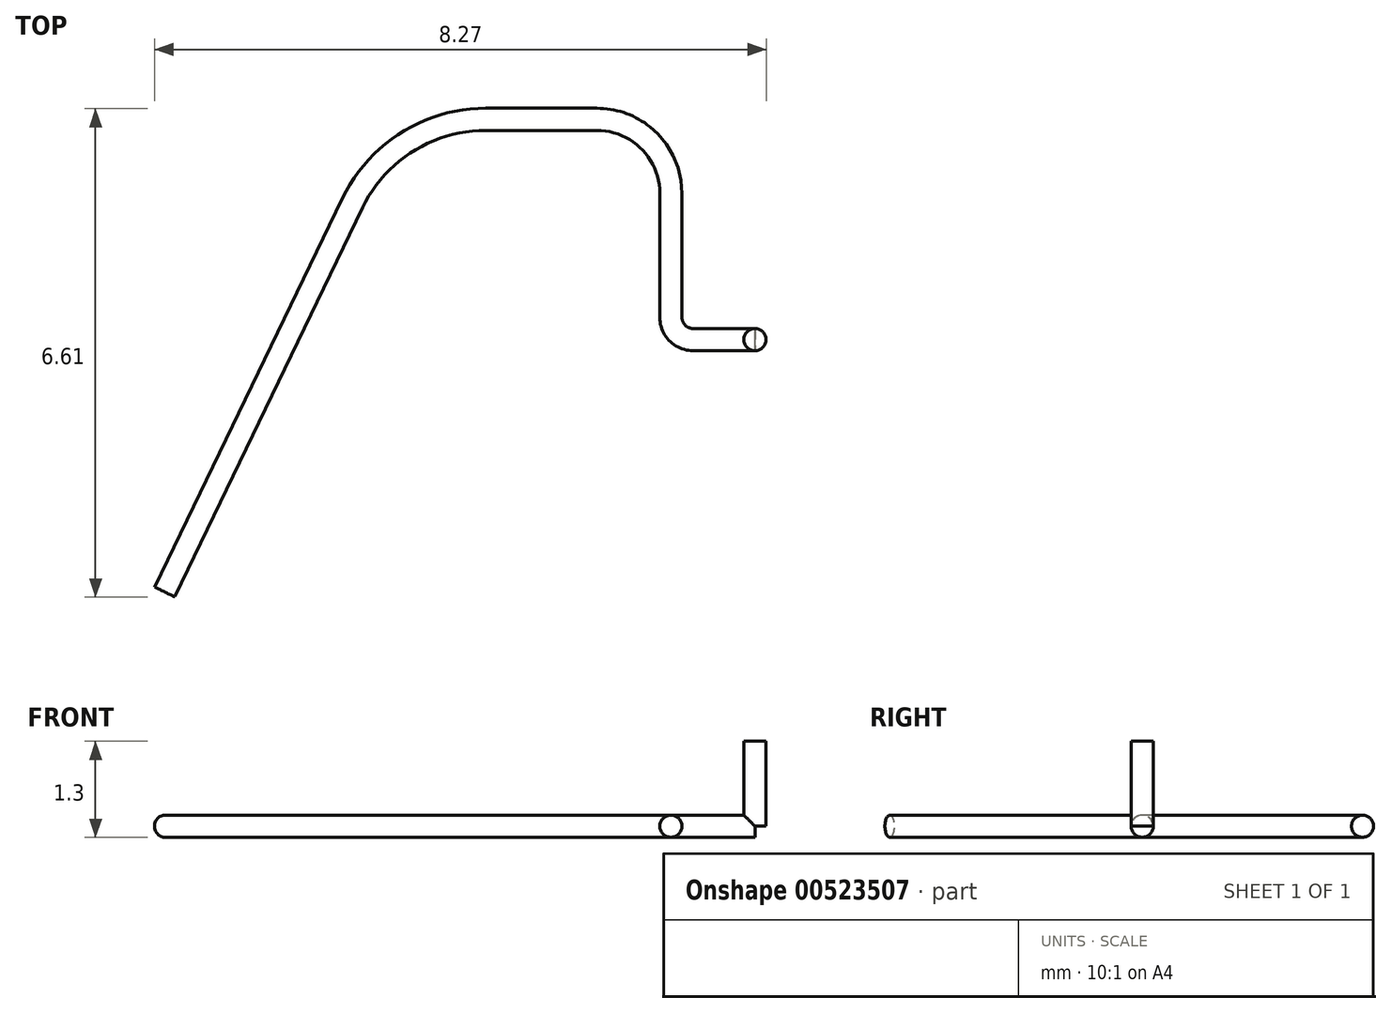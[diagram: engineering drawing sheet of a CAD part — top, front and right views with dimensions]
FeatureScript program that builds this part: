
annotation { "Feature Type Name" : "Feature", "Feature Type Description" : "" }
export const myFeature = defineFeature(function(context is Context, id is Id, definition is map)
    precondition{}
    {
        {
            var Q0;
            Q0=qCreatedBy(makeId("Front.planeOp"),FACE);
            var sketch = newSketch(context, id + "F0", { "sketchPlane" : qUnion([Q0])});
            skCircle(sketch, "E0", {"center": v(0, 0) * mm, "radius": 0.15 * mm});
            skSolve(sketch);
        }
        {
            var Q0;
            Q0=qCreatedBy(makeId("Top.planeOp"),FACE);
            var sketch = newSketch(context, id + "F1", { "sketchPlane" : qUnion([Q0])});
            skLineSegment(sketch, "E1", {"start": v(0, 0) * mm, "end": v(0, 1.08) * mm});
            skLineSegment(sketch, "E2", {"start": v(-1, 2.08) * mm, "end": v(-2.5, 2.08) * mm});
            skPoint(sketch, "E3.visualSharp", {"position": v(0, 2.08) * mm});
            skArc(sketch, "E3.filletArc", {"start": v(0, 1.08) * mm, "mid": v(-0.3, 1.8) * mm, "end": v(-1, 2.08) * mm});
            skLineSegment(sketch, "E4", {"start": v(-4.3, 0.95) * mm, "end": v(-6.85, -4.31) * mm});
            skPoint(sketch, "E5.visualSharp", {"position": v(-3.76, 2.08) * mm});
            skArc(sketch, "E5.filletArc", {"start": v(-2.5, 2.08) * mm, "mid": v(-3.57, 1.78) * mm, "end": v(-4.3, 0.95) * mm});
            skSolve(sketch);
        }
        {
            var Q0;
            Q0 = qSketchRegion(id + "F0", true);
            var Q1;
            Q1 = qConstructionFilter(qBodyType(qCreatedBy(id + "F1" ,EDGE), BodyType.WIRE), ConstructionObject.NO);
            sweep(context, id + "F2", {"profiles" : qUnion([Q0]), "path" : qUnion([Q1])});
        }
        {
            var Q0;
            Q0=qCreatedBy(makeId("Top.planeOp"),FACE);
            var sketch = newSketch(context, id + "F3", { "sketchPlane" : qUnion([Q0])});
            skLineSegment(sketch, "E6", {"start": v(0, 0) * mm, "end": v(0, -0.6) * mm});
            skLineSegment(sketch, "E7", {"start": v(0.3, -0.9) * mm, "end": v(1.14, -0.9) * mm});
            skPoint(sketch, "E8.visualSharp", {"position": v(0, -0.9) * mm});
            skArc(sketch, "E8.filletArc", {"start": v(0, -0.6) * mm, "mid": v(0.09, -0.8) * mm, "end": v(0.3, -0.9) * mm});
            skSolve(sketch);
        }
        {
            var Q0;
            Q0 = qSketchRegion(id + "F0", true);
            var Q1;
            Q1 = qConstructionFilter(qBodyType(qCreatedBy(id + "F3" ,EDGE), BodyType.WIRE), ConstructionObject.NO);
            sweep(context, id + "F4", {"operationType" : NewBodyOperationType.ADD, "profiles" : qUnion([Q0]), "path" : qUnion([Q1])});
        }
        {
            var Q0;
            Q0=makeQuery(id+"F4.opSweep","CAP_FACE",FACE,{"disambiguationData":[OSD([sQuery(id+"F0.wireOp",EDGE,"E0"),sQuery(id+"F3.wireOp",VERTEX,"E7.end")])],"isStart":false});
            var sketch = newSketch(context, id + "F5", { "sketchPlane" : qUnion([Q0])});
            skLineSegment(sketch, "E9", {"start": v(-0.9, 0) * mm, "end": v(-0.9, 1.15) * mm});
            skSolve(sketch);
        }
        {
            var Q0;
            Q0=qCreatedBy(makeId("Top.planeOp"),FACE);
            var sketch = newSketch(context, id + "F6", { "sketchPlane" : qUnion([Q0])});
            skCircle(sketch, "E10", {"center": v(1.14, -0.9) * mm, "radius": 0.15 * mm});
            skSolve(sketch);
        }
        {
            var Q0;
            Q0=makeQuery(id+"F6.imprint","IMPRINT",FACE,{"disambiguationData":[TD([[makeQuery(id+"F6.imprint","IMPRINT",EDGE,{"derivedFrom":sQuery(id+"F6.wireOp",EDGE,"E10")}),1.0]])]});
            var Q1;
            Q1=sQuery(id+"F5.wireOp",EDGE,"E9");
            sweep(context, id + "F7", {"operationType" : NewBodyOperationType.ADD, "profiles" : qUnion([Q0]), "path" : qUnion([Q1])});
        }
    });
